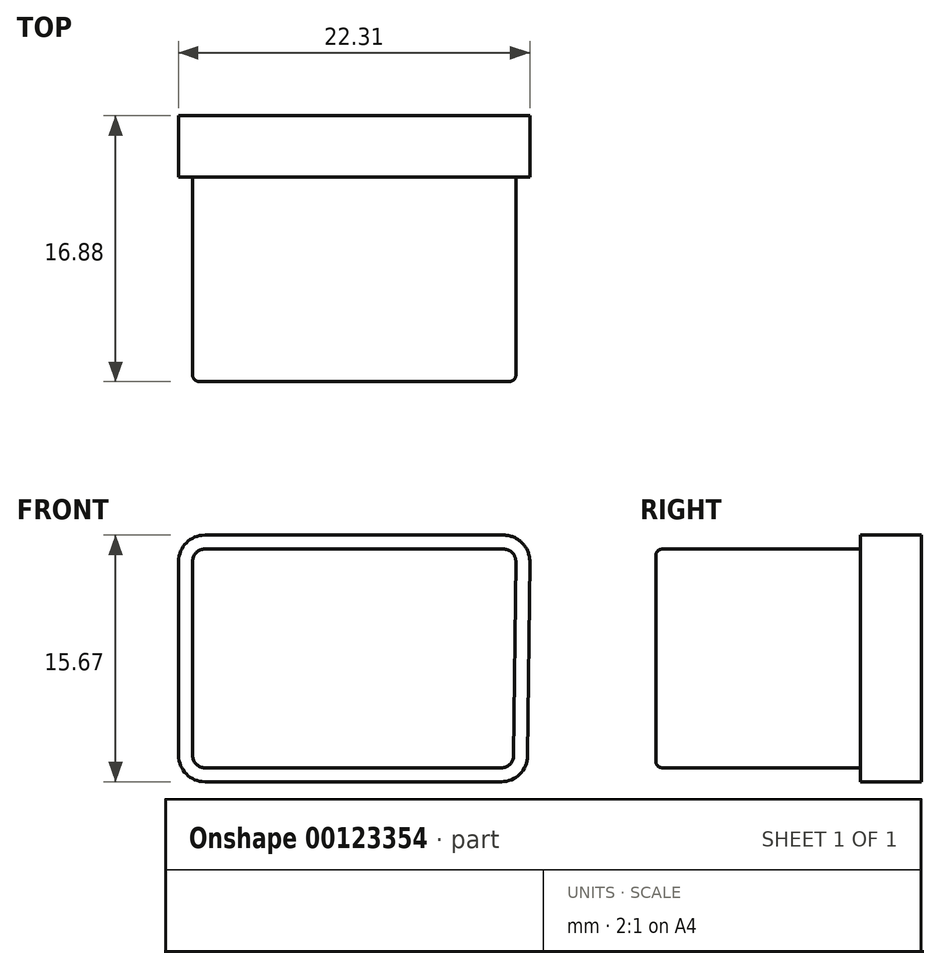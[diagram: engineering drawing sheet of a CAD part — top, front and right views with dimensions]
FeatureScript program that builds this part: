
annotation { "Feature Type Name" : "Feature", "Feature Type Description" : "" }
export const myFeature = defineFeature(function(context is Context, id is Id, definition is map)
    precondition{}
    {
        {
            var Q0;
            Q0=qCreatedBy(makeId("Front.planeOp"),FACE);
            var sketch = newSketch(context, id + "F0", { "sketchPlane" : qUnion([Q0])});
            skArc(sketch, "E0.0", {"start": v(-9.45, 6.95) * mm, "mid": v(-10, 6.72) * mm, "end": v(-10.23, 6.16) * mm});
            skLineSegment(sketch, "E0.1", {"start": v(-10.23, 6.16) * mm, "end": v(-10.23, -6.16) * mm});
            skLineSegment(sketch, "E0.2", {"start": v(-9.45, 6.95) * mm, "end": v(9.51, 6.95) * mm});
            skArc(sketch, "E0.3", {"start": v(-10.23, -6.16) * mm, "mid": v(-10, -6.71) * mm, "end": v(-9.45, -6.94) * mm});
            skArc(sketch, "E0.4", {"start": v(10.3, 6.15) * mm, "mid": v(10.07, 6.71) * mm, "end": v(9.51, 6.95) * mm});
            skLineSegment(sketch, "E0.5", {"start": v(10.3, 6.15) * mm, "end": v(10.16, -6.17) * mm});
            skArc(sketch, "E0.6", {"start": v(9.38, -6.94) * mm, "mid": v(9.93, -6.72) * mm, "end": v(10.16, -6.17) * mm});
            skLineSegment(sketch, "E0.7", {"start": v(-9.45, -6.94) * mm, "end": v(9.38, -6.94) * mm});
            skSolve(sketch);
        }
        {
            var Q0;
            Q0=makeQuery(id+"F0.imprint","IMPRINT",FACE,{"disambiguationData":[TD([[makeQuery(id+"F0.imprint","IMPRINT",EDGE,{"derivedFrom":sQuery(id+"F0.wireOp",EDGE,"E0.0")}),1.0]])]});
            extrude(context, id + "F1", {"entities" : qUnion([Q0]), "depth" : 13 * mm});
        }
        {
            var Q0;
            Q0=makeQuery(id+"F1.opExtrude","CAP_FACE",FACE,{"disambiguationData":[OSD([sQuery(id+"F0.wireOp",EDGE,"E0.0"),sQuery(id+"F0.wireOp",EDGE,"E0.1"),sQuery(id+"F0.wireOp",EDGE,"E0.2"),sQuery(id+"F0.wireOp",EDGE,"E0.3"),sQuery(id+"F0.wireOp",EDGE,"E0.4"),sQuery(id+"F0.wireOp",EDGE,"E0.5"),sQuery(id+"F0.wireOp",EDGE,"E0.6"),sQuery(id+"F0.wireOp",EDGE,"E0.7")])],"isStart":true});
            var sketch = newSketch(context, id + "F2", { "sketchPlane" : qUnion([Q0])});
            skArc(sketch, "E1.0", {"start": v(-10.3, 6.15) * mm, "mid": v(-10.07, 6.71) * mm, "end": v(-9.51, 6.95) * mm});
            skLineSegment(sketch, "E2.0", {"start": v(-10.3, 6.15) * mm, "end": v(-10.16, -6.17) * mm});
            skArc(sketch, "E3.0", {"start": v(-9.38, -6.94) * mm, "mid": v(-9.93, -6.72) * mm, "end": v(-10.16, -6.17) * mm});
            skLineSegment(sketch, "E4.0", {"start": v(9.45, -6.94) * mm, "end": v(-9.38, -6.94) * mm});
            skArc(sketch, "E5.0", {"start": v(10.23, -6.16) * mm, "mid": v(10, -6.71) * mm, "end": v(9.45, -6.94) * mm});
            skLineSegment(sketch, "E6.0", {"start": v(10.23, 6.16) * mm, "end": v(10.23, -6.16) * mm});
            skArc(sketch, "E7.0", {"start": v(9.45, 6.95) * mm, "mid": v(10, 6.72) * mm, "end": v(10.23, 6.16) * mm});
            skLineSegment(sketch, "E8.0", {"start": v(9.45, 6.95) * mm, "end": v(-9.51, 6.95) * mm});
            skArc(sketch, "E9.0", {"start": v(11.12, 6.16) * mm, "mid": v(10.63, 7.35) * mm, "end": v(9.45, 7.84) * mm});
            skLineSegment(sketch, "E9.1", {"start": v(11.12, -6.16) * mm, "end": v(11.12, 6.16) * mm});
            skLineSegment(sketch, "E9.2", {"start": v(9.45, 7.84) * mm, "end": v(-9.51, 7.84) * mm});
            skArc(sketch, "E9.3", {"start": v(9.45, -7.83) * mm, "mid": v(10.63, -7.34) * mm, "end": v(11.12, -6.16) * mm});
            skArc(sketch, "E9.4", {"start": v(-9.51, 7.84) * mm, "mid": v(-10.7, 7.34) * mm, "end": v(-11.19, 6.14) * mm});
            skLineSegment(sketch, "E9.5", {"start": v(-11.19, 6.14) * mm, "end": v(-11.05, -6.18) * mm});
            skArc(sketch, "E9.6", {"start": v(-11.05, -6.18) * mm, "mid": v(-10.55, -7.35) * mm, "end": v(-9.38, -7.83) * mm});
            skLineSegment(sketch, "E9.7", {"start": v(-9.38, -7.83) * mm, "end": v(9.45, -7.83) * mm});
            skSolve(sketch);
        }
        {
            var Q0;
            Q0=makeQuery(id+"F2.imprint","IMPRINT",FACE,{"disambiguationData":[TD([[makeQuery(id+"F2.imprint","IMPRINT",EDGE,{"derivedFrom":sQuery(id+"F2.wireOp",EDGE,"E1.0")}),1.0]])]});
            var Q1;
            Q1=makeQuery(id+"F2.imprint","IMPRINT",FACE,{"disambiguationData":[TD([[makeQuery(id+"F2.imprint","IMPRINT",EDGE,{"derivedFrom":sQuery(id+"F2.wireOp",EDGE,"E1.0")}),-1.0]])]});
            extrude(context, id + "F3", {"entities" : qUnion([Q0, Q1]), "operationType" : NewBodyOperationType.ADD, "depth" : 3.9 * mm});
        }
        {
            var Q0;
            Q0=makeQuery(id+"F1.opExtrude","CAP_FACE",FACE,{"disambiguationData":[OSD([sQuery(id+"F0.wireOp",EDGE,"E0.0"),sQuery(id+"F0.wireOp",EDGE,"E0.1"),sQuery(id+"F0.wireOp",EDGE,"E0.2"),sQuery(id+"F0.wireOp",EDGE,"E0.3"),sQuery(id+"F0.wireOp",EDGE,"E0.4"),sQuery(id+"F0.wireOp",EDGE,"E0.5"),sQuery(id+"F0.wireOp",EDGE,"E0.6"),sQuery(id+"F0.wireOp",EDGE,"E0.7")])],"isStart":false});
            fillet(context, id + "F4", {"entities" : qUnion([Q0]), "radius" : 0.4 * mm, "tangentPropagation" : true, "allowEdgeOverflow" : false});
        }
    });
